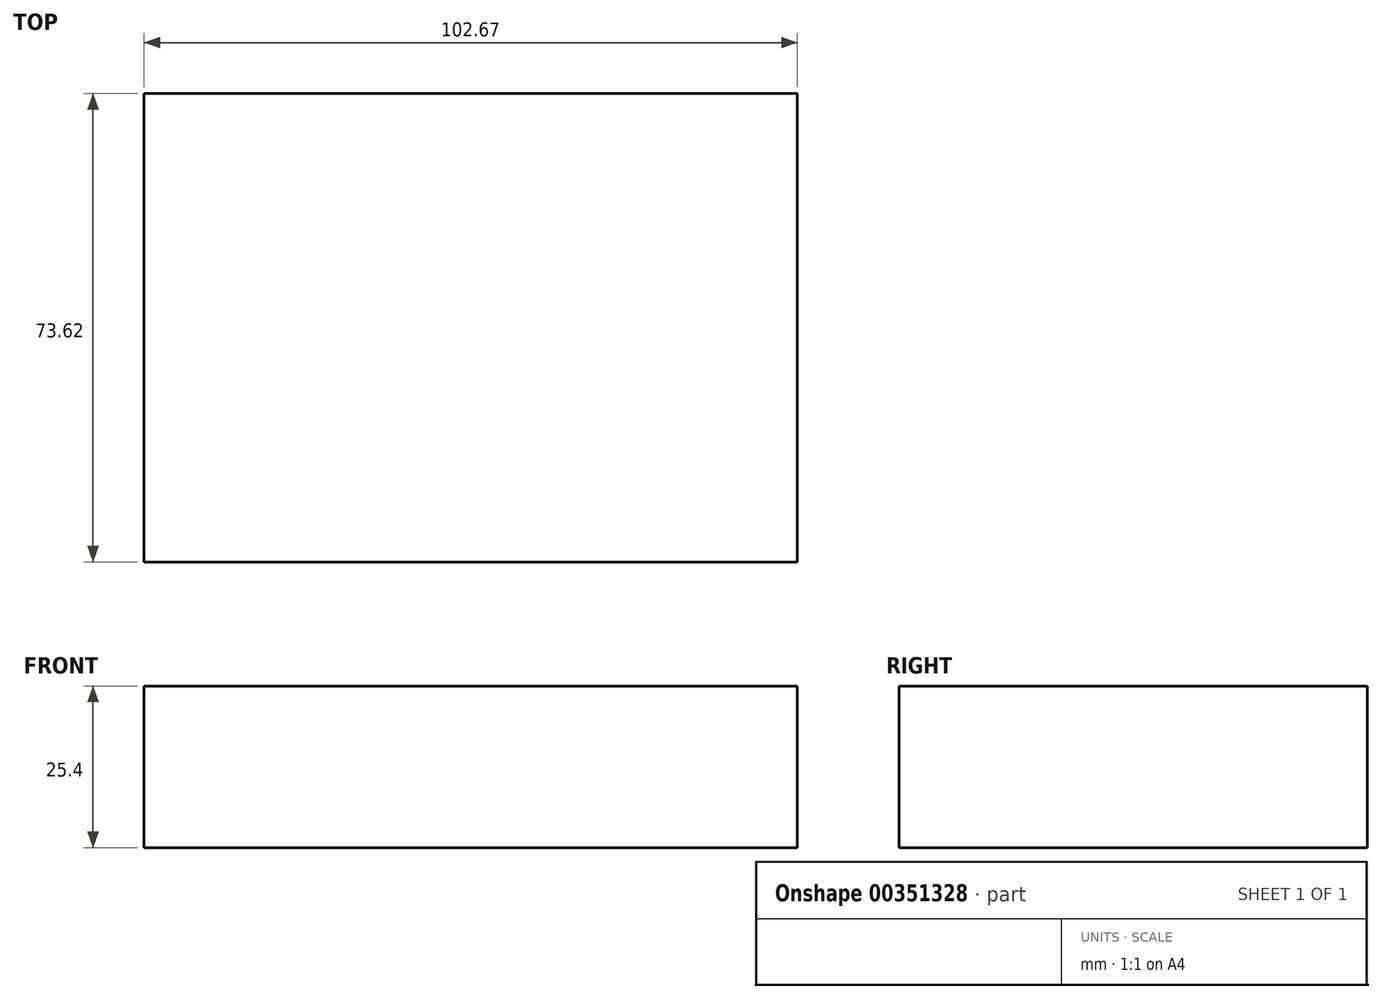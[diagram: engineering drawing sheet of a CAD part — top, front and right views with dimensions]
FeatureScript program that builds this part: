
annotation { "Feature Type Name" : "Feature", "Feature Type Description" : "" }
export const myFeature = defineFeature(function(context is Context, id is Id, definition is map)
    precondition{}
    {
        {
            var Q0;
            Q0=qCreatedBy(makeId("Top.planeOp"),FACE);
            var sketch = newSketch(context, id + "F0", { "sketchPlane" : qUnion([Q0])});
            skLineSegment(sketch, "E0", {"start": v(-54.84, -34.18) * mm, "end": v(-54.84, 39.44) * mm});
            skLineSegment(sketch, "E1", {"start": v(-54.84, 39.44) * mm, "end": v(47.83, 39.44) * mm});
            skLineSegment(sketch, "E2", {"start": v(47.83, 39.44) * mm, "end": v(47.83, -34.18) * mm});
            skLineSegment(sketch, "E3", {"start": v(47.83, -34.18) * mm, "end": v(-54.84, -34.18) * mm});
            skSolve(sketch);
        }
        {
            var Q0;
            Q0=makeQuery(id+"F0.imprint","IMPRINT",FACE,{"disambiguationData":[TD([[makeQuery(id+"F0.imprint","IMPRINT",EDGE,{"derivedFrom":sQuery(id+"F0.wireOp",EDGE,"E0")}),-1.0]])]});
            extrude(context, id + "F1", {"entities" : qUnion([Q0]), "depth" : 25.4 * mm});
        }
    });
